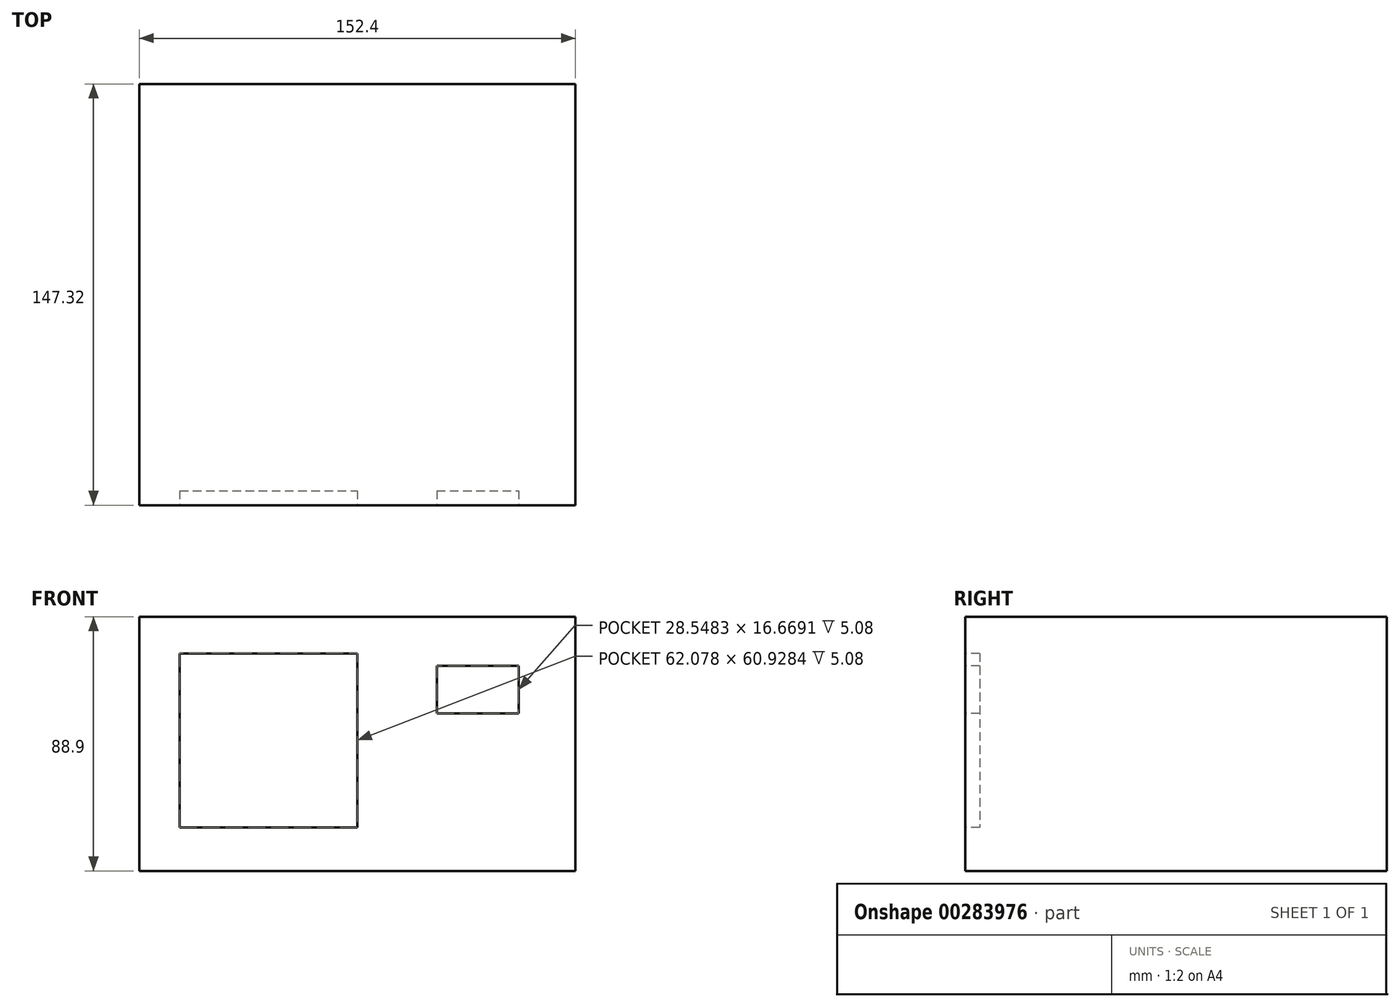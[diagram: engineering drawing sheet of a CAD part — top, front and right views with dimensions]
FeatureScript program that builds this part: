
annotation { "Feature Type Name" : "Feature", "Feature Type Description" : "" }
export const myFeature = defineFeature(function(context is Context, id is Id, definition is map)
    precondition{}
    {
        {
            var Q0;
            Q0=qCreatedBy(makeId("Top.planeOp"),FACE);
            var sketch = newSketch(context, id + "F0", { "sketchPlane" : qUnion([Q0])});
            skLineSegment(sketch, "E0.bottom", {"start": v(0, 0) * mm, "end": v(152.4, 0) * mm});
            skLineSegment(sketch, "E0.top", {"start": v(0, 147.32) * mm, "end": v(152.4, 147.32) * mm});
            skLineSegment(sketch, "E0.left", {"start": v(0, 0) * mm, "end": v(0, 147.32) * mm});
            skLineSegment(sketch, "E0.right", {"start": v(152.4, 0) * mm, "end": v(152.4, 147.32) * mm});
            skSolve(sketch);
        }
        {
            var Q0;
            Q0=makeQuery(id+"F0.imprint","IMPRINT",FACE,{"disambiguationData":[TD([[makeQuery(id+"F0.imprint","IMPRINT",EDGE,{"derivedFrom":sQuery(id+"F0.wireOp",EDGE,"E0.bottom")}),1.0]])]});
            extrude(context, id + "F1", {"entities" : qUnion([Q0]), "depth" : 88.9 * mm});
        }
        {
            var Q0;
            Q0=makeQuery(id+"F1.opExtrude","SWEPT_FACE",FACE,{"disambiguationData":[OSD([sQuery(id+"F0.wireOp",EDGE,"E0.bottom")])]});
            var sketch = newSketch(context, id + "F2", { "sketchPlane" : qUnion([Q0])});
            skLineSegment(sketch, "E1.bottom", {"start": v(14.1, 76.09) * mm, "end": v(76.18, 76.09) * mm});
            skLineSegment(sketch, "E1.top", {"start": v(14.1, 15.16) * mm, "end": v(76.18, 15.16) * mm});
            skLineSegment(sketch, "E1.left", {"start": v(14.1, 76.09) * mm, "end": v(14.1, 15.16) * mm});
            skLineSegment(sketch, "E1.right", {"start": v(76.18, 76.09) * mm, "end": v(76.18, 15.16) * mm});
            skLineSegment(sketch, "E2.bottom", {"start": v(103.96, 71.68) * mm, "end": v(132.51, 71.68) * mm});
            skLineSegment(sketch, "E2.top", {"start": v(103.96, 55.01) * mm, "end": v(132.51, 55.01) * mm});
            skLineSegment(sketch, "E2.left", {"start": v(103.96, 71.68) * mm, "end": v(103.96, 55.01) * mm});
            skLineSegment(sketch, "E2.right", {"start": v(132.51, 71.68) * mm, "end": v(132.51, 55.01) * mm});
            skSolve(sketch);
        }
        {
            var Q0;
            Q0=makeQuery(id+"F2.imprint","IMPRINT",FACE,{"disambiguationData":[TD([[makeQuery(id+"F2.imprint","IMPRINT",EDGE,{"derivedFrom":sQuery(id+"F2.wireOp",EDGE,"E1.bottom")}),-1.0]])]});
            var Q1;
            Q1=makeQuery(id+"F2.imprint","IMPRINT",FACE,{"disambiguationData":[TD([[makeQuery(id+"F2.imprint","IMPRINT",EDGE,{"derivedFrom":sQuery(id+"F2.wireOp",EDGE,"E2.bottom")}),-1.0]])]});
            extrude(context, id + "F3", {"entities" : qUnion([Q0, Q1]), "operationType" : NewBodyOperationType.REMOVE, "oppositeDirection" : true, "depth" : 5.08 * mm});
        }
    });
